# Revit family: Poly Max - Ceiling Clouds
name_source: partatom
category: Specialty Equipment
units: mm (PartAtom-declared; Revit-internal decimal feet)

## family parameters
Always vertical = No
Cut with Voids When Loaded = No
Enable Cutting in Views = Yes
Maintain Annotation Orientation = No
OmniClass Number = 23.35.00.00
OmniClass Title = Covering, Cladding, and Finishes
Part Type = Normal
Room Calculation Point = No
Round Connector Dimension = Use Diameter
Shared = No
Work Plane-Based = Yes

## types (20) — shared parameters
A = 0' - 0"
Acoustics - NRC = Sound absorption varies from NRC 0.45 to 0.95 based on installation method used when tested per ASTM C423.
Assembly Code = C30
Default Elevation = 4' - 0"
Description = Acoustic Panels
Fire Rating = ASTM E84 - Class A
Manufacturer = Acoustical Surfaces, Inc.
Material = Poly Max
Model = Poly Max - Ceiling Panels
Recycled Content Percentage = 0%
Type Comments = Acoustic Panels
URL = https://www.acousticalsurfaces.com

## per-type parameters (varying)
| type | Finish | Length | T | Thickness Options | Width | ‍      1. Thickness 1" | ‍      2. Thickness 2" |
| 1 INCH THICK - 48X96 - Printed Grpahics | Paint - Acoustical-Surfaces - Printed Graphics | 8' - 0" | 0' - 1" | 1 | 4' - 0" | Yes | No |
| 1 INCH THICK - 48X96 - Silver | Paint - Acoustical-Surfaces - Silver | 8' - 0" | 0' - 1" | 1 | 4' - 0" | Yes | No |
| 1 INCH THICK - 48X96 - Black | Paint - Acoustical-Surfaces - Black | 8' - 0" | 0' - 1" | 1 | 4' - 0" | Yes | No |
| 1 INCH THICK - 48X96 - White | Paint - Acoustical-Surfaces - White | 8' - 0" | 0' - 1" | 1 | 4' - 0" | Yes | No |
| 2 INCH THICK - 48X96 - Printed Graphics | Paint - Acoustical-Surfaces - Printed Graphics | 8' - 0" | 0' - 2" | 2 | 4' - 0" | No | Yes |
| 2 INCH THICK - 48X96 - Silver | Paint - Acoustical-Surfaces - Silver | 8' - 0" | 0' - 2" | 2 | 4' - 0" | No | Yes |
| 2 INCH THICK - 48X96 - Black | Paint - Acoustical-Surfaces - Black | 8' - 0" | 0' - 2" | 2 | 4' - 0" | No | Yes |
| 2 INCH THICK - 48X96 - Beige | Paint - Acoustical-Surfaces - Beige | 8' - 0" | 0' - 2" | 2 | 4' - 0" | No | Yes |
| 2 INCH THICK - 48X96 - White | Paint - Acoustical-Surfaces - White | 8' - 0" | 0' - 2" | 2 | 4' - 0" | No | Yes |
| 2 INCH THICK - 24x48 - Printed Graphics | Paint - Acoustical-Surfaces - Printed Graphics | 4' - 0" | 0' - 0 1/2" | 0 | 2' - 0" | No | No |
| 2 INCH THICK - 24x48 - Silver | Paint - Acoustical-Surfaces - Silver | 4' - 0" | 0' - 0 1/2" | 0 | 2' - 0" | No | No |
| 2 INCH THICK - 24x48 - Black | Paint - Acoustical-Surfaces - Black | 4' - 0" | 0' - 0 1/2" | 0 | 2' - 0" | No | No |
| 2 INCH THICK - 24x48 - White | Paint - Acoustical-Surfaces - White | 4' - 0" | 0' - 0 1/2" | 0 | 2' - 0" | No | No |
| 1 INCH THICK - 24x48 - Silver | Paint - Acoustical-Surfaces - Silver | 4' - 0" | 0' - 1" | 1 | 2' - 0" | Yes | No |
| 1 INCH THICK - 24x48 - Black | Paint - Acoustical-Surfaces - Black | 4' - 0" | 0' - 1" | 1 | 2' - 0" | Yes | No |
| 1 INCH THICK - 24x48 - Beige | Paint - Acoustical-Surfaces - Beige | 4' - 0" | 0' - 1" | 1 | 2' - 0" | Yes | No |
| 1 INCH THICK - 24x48 - White | Paint - Acoustical-Surfaces - White | 4' - 0" | 0' - 1" | 1 | 2' - 0" | Yes | No |
| 2 INCH THICK - 24x48 - Beige | Paint - Acoustical-Surfaces - Beige | 4' - 0" | 0' - 0 1/2" | 0 | 2' - 0" | No | No |
| 1 INCH THICK - 24x48 - Printed Graphics | Paint - Acoustical-Surfaces - Printed Graphics | 4' - 0" | 0' - 1" | 1 | 2' - 0" | Yes | No |
| 1 INCH THICK - 48X96 - Beige | Paint - Acoustical-Surfaces - Beige | 8' - 0" | 0' - 1" | 1 | 4' - 0" | Yes | No |

## geometry (parser evidence)
native form markers: Sweep x10
no freeform markers — native parametric forms only
